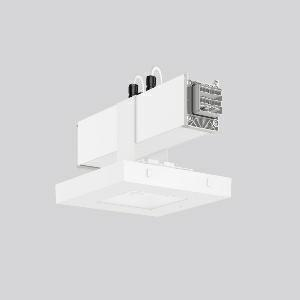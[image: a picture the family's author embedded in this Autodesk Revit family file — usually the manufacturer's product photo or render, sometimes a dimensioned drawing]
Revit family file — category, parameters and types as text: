
# Revit family: linedo_module_rf_9503rf_762_409_000_067e
name_source: partatom
category: Lighting Fixtures
units: mm (PartAtom-declared; Revit-internal decimal feet)

## family parameters
Cut with Voids When Loaded = No
Host = Face
Light Source = No
Part Type = Normal
Room Calculation Point = No
Round Connector Dimension = Use Diameter
Shared = No

## types (1)
- LINEDO Module RF (1 x LED Modul 765, 420 lm, 6500)
    Apparent Load = 7 VA
    CIE Flux Codes = 48 88 100 100 100
    Color Rendering = 70
    Color Temperature = 6500
    Default Elevation = 1800 mm
    Description = LINEDO, 6,7 W, 420 lm, 765, white, on/off
Continuous line luminaire, L 330 B 198 H 170, CBS, emergency-420 lm, AC-Control
    Height = 170 mm  [stored 0.557743 ft]
    Lamp = 1 x LED Modul 765
    Lamp Light Flux = 420 lm
    Lamp count = 1
    Length = 330 mm
    Lifetime = 50000 h
    Luminous efficacy = 63 lm/W
    Manufacturer = RZB
    ModVariant = No
    Model = 9503RF.762.409.000
    Mounting Place = Ceiling
    Mounting Type = Pendant, Surface mounted
    Number of Poles = 1
    OnlyDefault = Yes
    Power Factor = 1
    Product Name = LINEDO Module RF
    Product group = Surface mounted continuous line luminaire system
    ProductGroupID = 310
    Protection Class = Protection class I
    Protection Degree = IP 54
    RLX_Detail_Level = 1
    RLX_Emergency_Light_Flux = 420 lm
    RLX_Emergency_Type = 3
    RLX_Emergency_Type_DB = Yes
    RlxData = <blob elided: 19997 chars, md5=1ba0ce8d>
    Socket = socket
    Standby Power = 0 W
    System Light Flux = 420 lm
    System Power = 7 W
    Type Comments = Product without accessories
    Type Image = 9503rw.762.434.000.jpg
    URL = http://relux.com
    VarID = ---
    Voltage = 230 V
    Voltage Range = 220-240 V
    Weight = 0.00 kg
    Width = 198 mm

note: [stored X ft] marks values corroborated as IEEE doubles in the binary element streams (Revit-internal decimal feet)

## geometry (parser evidence)
native form markers: Blend x4, Sweep x12
no freeform markers — native parametric forms only
